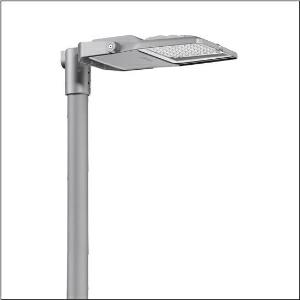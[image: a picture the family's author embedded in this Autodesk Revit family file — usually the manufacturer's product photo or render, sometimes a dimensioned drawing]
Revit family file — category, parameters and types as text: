
# Revit family: floodlight_fl_21_iq_mini___pl52_5xa7771b2d3a_cd8f
name_source: partatom
category: Lighting Fixtures
units: mm (PartAtom-declared; Revit-internal decimal feet)

## family parameters
Cut with Voids When Loaded = No
Host = Face
Light Source = No
Part Type = Normal
Room Calculation Point = No
Round Connector Dimension = Use Diameter
Shared = No

## types (1)
- --- (1 x LED, 6240 lm, 45.5 W, 3000K)
    Apparent Load = 46 VA
    CIE Flux Codes = 26 60 98 100 100
    Color Rendering = 70
    Color Temperature = 3000K
    Default Elevation = 1800 mm
    Description = Floodlight FL 21 iQ mini, floodlight, primary light control with lens, of PMMA, primary optical cover: protective disc, of toughened safety glass, transparent, light distribution: PL52, light emission: direct distribution, installation type: surface-mounted, LED, High Power LED, rated luminous flux: 6.240lm, luminous efficacy: 137lm/W, light colour: 730, colour temperature: 3000K, control: Auto-Match, Temp-Guard, Lumen-Switch, Night-Set, Smart-Wire, Light-Fading, Desk-Remote (wireless, voltage-free reading and setting of iQ features in the workshop via application-optimized NFC function/RFID function), optimised constant luminous flux control (CLO 2.0), with terminal, 6-pole, mains connection: 220..240V, AC, 50/60Hz, start of lifetime: 46W, end of service life: 48W, reduction: 22W, luminaire housing, of diecast aluminium, powder-coated, Siteco® metallic grey (DB 702S), corrosivity category C5 mid according to DIN EN ISO 12944, sealing non-destructively replaceable, please order mast flange separately, mast bracket, of steel, galvanised, powder-coated, Siteco® metallic grey (DB 702S), protection rating (complete): IP66, insulation class (complete): insulation class II (safety insulation), certification: CE, ENEC, VDE, protection symbol: D, impact resistance: IK08, permissible operating ambient temperature: -40..+40°C, permissible operating ambient temperature for outdoor applications: -40..+50°C, standard: DIN EN 12944, LABS conformity tested according to VDMA 24364:2018-05, packaging unit: 1 piece

Light Distribution: PL52
    Height = 70 mm
    Lamp = 1 x LED
    Lamp Light Flux = 6240 lm
    Lamp Power = 45.5 W
    Lamp count = 1
    Length = 485 mm
    Luminous efficacy = 137 lm/W
    Manufacturer = Siteco
    ModVariant = No
    Model = 5XA7771B2D3A
    Number of Poles = 1
    OnlyDefault = Yes
    Power Factor = 1
    Product Name = Floodlight FL 21 iQ mini | PL52
    Product group = floodlight | pylon annexe
    ProductGroupID = 6200
    Protection Class = Protection class II
    Protection Degree = IP 66
    RLX_Detail_Level = 1
    RLX_Emergency_Light_Flux = 0 lm
    RLX_Emergency_Type = 0
    RLX_Emergency_Type_DB = No
    RlxData = <blob elided: 101329 chars, md5=9fae8d90>
    Socket = socket
    Standby Power = 0 W
    System Light Flux = 6240 lm
    System Power = 46 W
    Type Comments = factory setting: luminous flux: 100 % | dim-lin: 254 | 463 mA
    Type Image = l_1007125.jpg
    URL = http://relux.com
    VarID = @adj_097395
    Voltage = 0 V
    Weight = 0.00 kg
    Width = 337 mm

## geometry (parser evidence)
native form markers: Blend x4, Sweep x12
no freeform markers — native parametric forms only
